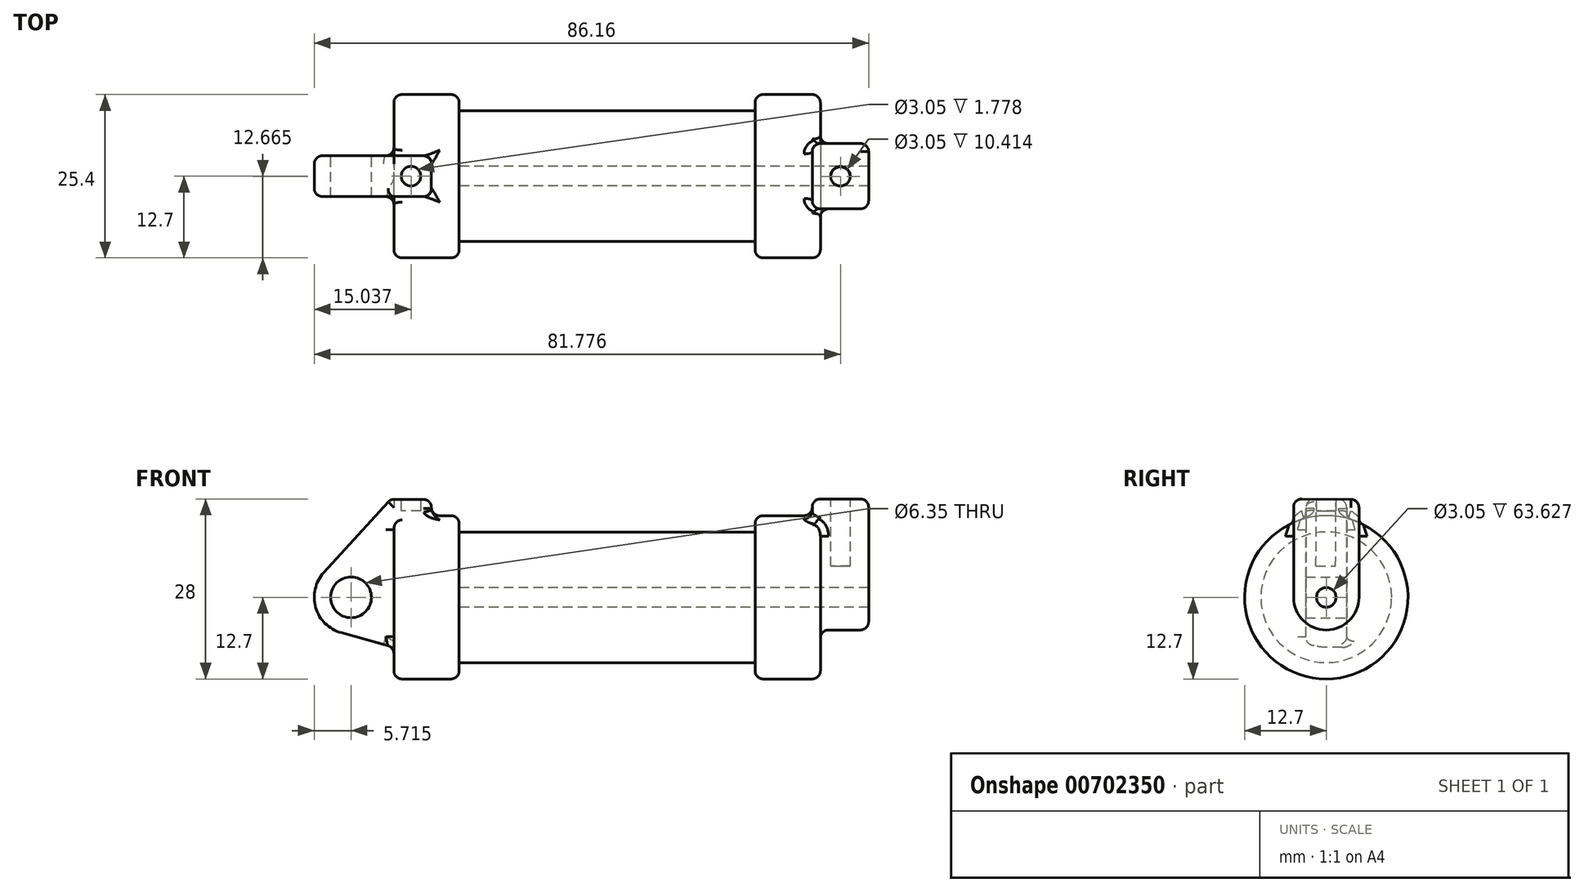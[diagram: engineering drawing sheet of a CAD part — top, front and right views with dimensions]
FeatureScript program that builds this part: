
annotation { "Feature Type Name" : "Feature", "Feature Type Description" : "" }
export const myFeature = defineFeature(function(context is Context, id is Id, definition is map)
    precondition{}
    {
        {
            var Q0;
            Q0=qCreatedBy(makeId("Front.planeOp"),FACE);
            var sketch = newSketch(context, id + "F0", { "sketchPlane" : qUnion([Q0])});
            skLineSegment(sketch, "E0", {"start": v(0, 0) * mm, "end": v(0, 12.7) * mm});
            skLineSegment(sketch, "E1", {"start": v(0, 12.7) * mm, "end": v(10.16, 12.7) * mm});
            skLineSegment(sketch, "E2", {"start": v(10.16, 12.7) * mm, "end": v(10.16, 10.16) * mm});
            skLineSegment(sketch, "E3", {"start": v(10.16, 10.16) * mm, "end": v(56.13, 10.16) * mm});
            skLineSegment(sketch, "E4", {"start": v(56.13, 10.16) * mm, "end": v(56.13, 12.7) * mm});
            skLineSegment(sketch, "E5", {"start": v(56.13, 12.7) * mm, "end": v(66.3, 12.7) * mm});
            skLineSegment(sketch, "E6", {"start": v(66.3, 12.7) * mm, "end": v(66.3, 0) * mm});
            skLineSegment(sketch, "E7", {"start": v(66.3, 0) * mm, "end": v(0, 0) * mm});
            skLineSegment(sketch, "E8", {"start": v(5.84, 15.24) * mm, "end": v(-0.5, 15.24) * mm});
            skLineSegment(sketch, "E9", {"start": v(-0.5, 15.24) * mm, "end": v(-10.88, 3.85) * mm});
            skLineSegment(sketch, "E10", {"start": v(0, 0) * mm, "end": v(-6.65, 0) * mm});
            skCircle(sketch, "E11", {"center": v(-6.65, 0) * mm, "radius": 5.72 * mm});
            skCircle(sketch, "E12", {"center": v(-6.65, 0) * mm, "radius": 3.18 * mm});
            skLineSegment(sketch, "E13", {"start": v(5.84, 15.24) * mm, "end": v(5.84, -9.4) * mm});
            skLineSegment(sketch, "E14", {"start": v(5.84, -9.4) * mm, "end": v(-8.18, -5.5) * mm});
            skSolve(sketch);
        }
        {
            var Q0;
            {var subQ0=sQuery(id+"F0.wireOp",EDGE,"E0");Q0=makeQuery(id+"F0.imprint","IMPRINT",FACE,{"disambiguationData":[TD([[makeQuery(id+"F0.imprint","IMPRINT",EDGE,{"derivedFrom":subQ0}),-1.0]])]});}
            var Q1;
            {var subQ1=sQuery(id+"F0.wireOp",EDGE,"E0");Q1=makeQuery(id+"F0.imprint","IMPRINT",FACE,{"disambiguationData":[TD([[makeQuery(id+"F0.imprint","IMPRINT",EDGE,{"derivedFrom":subQ1}),1.0]])]});}
            var Q2;
            {var subQ0=sQuery(id+"F0.wireOp",EDGE,"E14");Q2=makeQuery(id+"F0.imprint","IMPRINT",FACE,{"disambiguationData":[TD([[makeQuery(id+"F0.imprint","IMPRINT",EDGE,{"derivedFrom":subQ0}),-1.0]])]});}
            var Q3;
            {var subQ5=sQuery(id+"F0.wireOp",EDGE,"E12");Q3=makeQuery(id+"F0.imprint","IMPRINT",FACE,{"disambiguationData":[TD([[makeQuery(id+"F0.imprint","IMPRINT",EDGE,{"derivedFrom":subQ5}),-1.0]])]});}
            extrude(context, id + "F1", {"entities" : qUnion([Q0, Q1, Q2, Q3]), "endBound" : BoundingType.SYMMETRIC, "depth" : 6.35 * mm, "offsetDistance" : 25.4 * mm});
        }
        {
            var Q0;
            {var subQ0=sQuery(id+"F0.wireOp",EDGE,"E0");Q0=makeQuery(id+"F0.imprint","IMPRINT",FACE,{"disambiguationData":[TD([[makeQuery(id+"F0.imprint","IMPRINT",EDGE,{"derivedFrom":subQ0}),-1.0]])]});}
            var Q1;
            {var subQ0=sQuery(id+"F0.wireOp",EDGE,"E2");Q1=makeQuery(id+"F0.imprint","IMPRINT",FACE,{"disambiguationData":[TD([[makeQuery(id+"F0.imprint","IMPRINT",EDGE,{"derivedFrom":subQ0}),-1.0]])]});}
            var Q2;
            Q2=sQuery(id+"F0.wireOp",EDGE,"E7");
            revolve(context, id + "F2", {"operationType" : NewBodyOperationType.ADD, "entities" : qUnion([Q0, Q1]), "axis" : qUnion([Q2]), "revolveType" : RevolveType.FULL});
        }
        {
            var Q0;
            Q0=makeQuery(id+"F2.opRevolve","SWEPT_FACE",FACE,{"disambiguationData":[OSD([sQuery(id+"F0.wireOp",EDGE,"E6")])]});
            var sketch = newSketch(context, id + "F3", { "sketchPlane" : qUnion([Q0])});
            skCircle(sketch, "E15", {"center": v(0, 0) * mm, "radius": 1.52 * mm});
            skCircle(sketch, "E16", {"center": v(0, 0) * mm, "radius": 5.08 * mm});
            skLineSegment(sketch, "E17", {"start": v(-5.08, 0) * mm, "end": v(-5.08, 15.3) * mm});
            skLineSegment(sketch, "E18", {"start": v(5.08, 0) * mm, "end": v(5.08, 15.24) * mm});
            skLineSegment(sketch, "E19", {"start": v(-5.08, 15.3) * mm, "end": v(5.08, 15.24) * mm});
            skSolve(sketch);
        }
        {
            var Q0;
            {var subQ2=sQuery(id+"F3.wireOp",EDGE,"E19");Q0=makeQuery(id+"F3.imprint","IMPRINT",FACE,{"disambiguationData":[TD([[makeQuery(id+"F3.imprint","IMPRINT",EDGE,{"derivedFrom":subQ2}),-1.0]])]});}
            var Q1;
            {var subQ3=sQuery(id+"F0.wireOp",EDGE,"E6");var subQ11=makeQuery(id+"F1.opExtrude","CAP_EDGE",EDGE,{"disambiguationData":[OSD([subQ3])],"isStart":true});Q1=makeQuery(id+"F3.imprint","IMPRINT",FACE,{"disambiguationData":[TD([[makeQuery(id+"F3.imprint","IMPRINT",EDGE,{"derivedFrom":subQ11}),-1.0]])]});}
            var Q2;
            Q2=makeQuery(id+"F3.imprint","IMPRINT",FACE,{"disambiguationData":[TD([[makeQuery(id+"F3.imprint","IMPRINT",EDGE,{"derivedFrom":sQuery(id+"F3.wireOp",EDGE,"E15")}),-1.0]])]});
            var Q3;
            {var subQ0=sQuery(id+"F3.wireOp",EDGE,"E17");var subQ1=sQuery(id+"F3.wireOp",EDGE,"E16");var subQ2=makeQuery(id+"F3.imprint","INTERSECT",VERTEX,{"derivedFrom":[subQ1,subQ0]});Q3=makeQuery(id+"F3.imprint","IMPRINT",FACE,{"disambiguationData":[TD([[makeQuery(id+"F3.imprint","IMPRINT",EDGE,{"disambiguationData":[TD([[subQ2,1.0]])],"derivedFrom":subQ1}),-1.0]])]});}
            extrude(context, id + "F4", {"entities" : qUnion([Q0, Q1, Q2, Q3]), "operationType" : NewBodyOperationType.ADD, "depth" : 7.5 * mm, "offsetDistance" : 25.4 * mm, "hasSecondDirection" : true, "secondDirectionOppositeDirection" : true, "secondDirectionDepth" : 1.27 * mm});
        }
        {
            var Q0;
            {var subQ0=sQuery(id+"F0.wireOp",EDGE,"E6");Q0=makeQuery(id+"F4.boolean.opBoolean","SPLIT",FACE,{"disambiguationData":[TD([makeQuery(id+"F4.opExtrude","SWEPT_FACE",FACE,{"disambiguationData":[OSD([sQuery(id+"F3.wireOp",EDGE,"E15")])]})])],"derivedFrom":makeQuery(id+"F2.boolean.opBoolean","MERGE",FACE,{"derivedFrom":[makeQuery(id+"F1.opExtrude","SWEPT_FACE",FACE,{"disambiguationData":[OSD([subQ0])]}),makeQuery(id+"F2.opRevolve","SWEPT_FACE",FACE,{"disambiguationData":[OSD([subQ0])]})]})});}
            var Q1;
            {var subQ0=sQuery(id+"F0.wireOp",EDGE,"E2");Q1=makeQuery(id+"F2.boolean.opBoolean","MERGE",FACE,{"derivedFrom":[makeQuery(id+"F1.opExtrude","SWEPT_FACE",FACE,{"disambiguationData":[OSD([subQ0])]}),makeQuery(id+"F2.opRevolve","SWEPT_FACE",FACE,{"disambiguationData":[OSD([subQ0])]})]});}
            extrude(context, id + "F5", {"entities" : qUnion([Q0]), "operationType" : NewBodyOperationType.REMOVE, "endBound" : BoundingType.UP_TO_SURFACE, "oppositeDirection" : true, "depth" : 25.4 * mm, "endBoundEntityFace" : qUnion([Q1]), "offsetDistance" : 25.4 * mm});
        }
        {
            var Q0;
            Q0=makeQuery(id+"F1.opExtrude","SWEPT_FACE",FACE,{"disambiguationData":[OSD([sQuery(id+"F0.wireOp",EDGE,"E8")])]});
            var sketch = newSketch(context, id + "F6", { "sketchPlane" : qUnion([Q0])});
            skCircle(sketch, "E20", {"center": v(2.67, 0) * mm, "radius": 1.52 * mm});
            skPoint(sketch, "E20.centerSnap0", {"position": v(2.67, 3.18) * mm});
            skPoint(sketch, "E20.centerSnap1", {"position": v(-0.5, 0) * mm});
            skSolve(sketch);
        }
        {
            var Q0;
            Q0=makeQuery(id+"F4.opExtrude","SWEPT_FACE",FACE,{"disambiguationData":[OSD([sQuery(id+"F3.wireOp",EDGE,"E19")])]});
            var sketch = newSketch(context, id + "F7", { "sketchPlane" : qUnion([Q0])});
            skCircle(sketch, "E21", {"center": v(69.4, -0.1) * mm, "radius": 1.52 * mm});
            skPoint(sketch, "E21.centerSnap0", {"position": v(73.79, -0.1) * mm});
            skPoint(sketch, "E21.centerSnap1", {"position": v(69.4, 4.98) * mm});
            skSolve(sketch);
        }
        {
            var Q0;
            Q0 = qSketchRegion(id + "F6", true);
            extrude(context, id + "F8", {"entities" : qUnion([Q0]), "operationType" : NewBodyOperationType.REMOVE, "oppositeDirection" : true, "depth" : 1.78 * mm, "offsetDistance" : 25.4 * mm});
        }
        {
            var Q0;
            Q0 = qSketchRegion(id + "F7", true);
            extrude(context, id + "F9", {"entities" : qUnion([Q0]), "operationType" : NewBodyOperationType.REMOVE, "oppositeDirection" : true, "depth" : 10.4 * mm, "offsetDistance" : 25.4 * mm});
        }
        {
            var Q0;
            Q0=makeQuery(id+"F2.opRevolve","SWEPT_EDGE",EDGE,{"disambiguationData":[OSD([sQuery(id+"F0.wireOp",EDGE,"E1"),sQuery(id+"F0.wireOp",EDGE,"E2")])]});
            fillet(context, id + "F10", {"entities" : qUnion([Q0]), "radius" : 1.27 * mm, "tangentPropagation" : true, "allowEdgeOverflow" : false});
        }
        {
            var Q0;
            Q0=makeQuery(id+"F2.opRevolve","SWEPT_EDGE",EDGE,{"disambiguationData":[OSD([sQuery(id+"F0.wireOp",EDGE,"E4"),sQuery(id+"F0.wireOp",EDGE,"E5")])]});
            fillet(context, id + "F11", {"entities" : qUnion([Q0]), "radius" : 1.27 * mm, "tangentPropagation" : true, "allowEdgeOverflow" : false});
        }
        {
            var Q0;
            Q0=makeQuery(id+"F4.opExtrude","SWEPT_EDGE",EDGE,{"disambiguationData":[OSD([sQuery(id+"F3.wireOp",EDGE,"E17"),sQuery(id+"F3.wireOp",EDGE,"E19")])]});
            fillet(context, id + "F12", {"entities" : qUnion([Q0]), "radius" : 1.27 * mm, "tangentPropagation" : true, "allowEdgeOverflow" : false});
        }
        {
            var Q0;
            Q0=makeQuery(id+"F4.opExtrude","CAP_EDGE",EDGE,{"disambiguationData":[OSD([sQuery(id+"F3.wireOp",EDGE,"E19")])],"isStart":false});
            fillet(context, id + "F13", {"entities" : qUnion([Q0]), "radius" : 1.27 * mm, "tangentPropagation" : true, "allowEdgeOverflow" : false});
        }
        {
            var Q0;
            Q0=makeQuery(id+"F2.opRevolve","SWEPT_EDGE",EDGE,{"disambiguationData":[OSD([sQuery(id+"F0.wireOp",EDGE,"E5"),sQuery(id+"F0.wireOp",EDGE,"E6")])]});
            fillet(context, id + "F14", {"entities" : qUnion([Q0]), "radius" : 1.27 * mm, "tangentPropagation" : true, "allowEdgeOverflow" : false});
        }
        {
            var Q0;
            Q0=makeQuery(id+"F4.opExtrude","SWEPT_EDGE",EDGE,{"disambiguationData":[OSD([sQuery(id+"F3.wireOp",EDGE,"E18"),sQuery(id+"F3.wireOp",EDGE,"E19")])]});
            fillet(context, id + "F15", {"entities" : qUnion([Q0]), "radius" : 1.27 * mm, "tangentPropagation" : true, "allowEdgeOverflow" : false});
        }
        {
            var Q0;
            Q0=makeQuery(id+"F4.boolean.opBoolean","INTERSECT",EDGE,{"derivedFrom":[makeQuery(id+"F2.opRevolve","SWEPT_FACE",FACE,{"disambiguationData":[OSD([sQuery(id+"F0.wireOp",EDGE,"E6")])]}),makeQuery(id+"F4.opExtrude","SWEPT_FACE",FACE,{"disambiguationData":[OSD([sQuery(id+"F3.wireOp",EDGE,"E17")])]})]});
            fillet(context, id + "F16", {"entities" : qUnion([Q0]), "radius" : 1.27 * mm, "tangentPropagation" : true, "allowEdgeOverflow" : false});
        }
        {
            var Q0;
            Q0=makeQuery(id+"F1.opExtrude","CAP_EDGE",EDGE,{"disambiguationData":[OSD([sQuery(id+"F0.wireOp",EDGE,"E8")])],"isStart":true});
            fillet(context, id + "F17", {"entities" : qUnion([Q0]), "radius" : 1.27 * mm, "tangentPropagation" : true, "allowEdgeOverflow" : false});
        }
        {
            var Q0;
            Q0=makeQuery(id+"F1.opExtrude","CAP_EDGE",EDGE,{"disambiguationData":[OSD([sQuery(id+"F0.wireOp",EDGE,"E9")])],"isStart":false});
            var Q1;
            Q1=makeQuery(id+"F2.boolean.opBoolean","INTERSECT",EDGE,{"derivedFrom":[makeQuery(id+"F1.opExtrude","CAP_FACE",FACE,{"disambiguationData":[OSD([sQuery(id+"F0.wireOp",EDGE,"E8"),sQuery(id+"F0.wireOp",EDGE,"E9"),sQuery(id+"F0.wireOp",EDGE,"E11"),sQuery(id+"F0.wireOp",EDGE,"E12"),sQuery(id+"F0.wireOp",EDGE,"E13"),sQuery(id+"F0.wireOp",EDGE,"E14")])],"isStart":false}),makeQuery(id+"F2.opRevolve","SWEPT_FACE",FACE,{"disambiguationData":[OSD([sQuery(id+"F0.wireOp",EDGE,"E0")])]})]});
            fillet(context, id + "F18", {"entities" : qUnion([Q0, Q1]), "radius" : 1.27 * mm, "tangentPropagation" : true, "allowEdgeOverflow" : false});
        }
        {
            var Q0;
            Q0=makeQuery(id+"F2.boolean.opBoolean","INTERSECT",EDGE,{"derivedFrom":[makeQuery(id+"F1.opExtrude","CAP_FACE",FACE,{"disambiguationData":[OSD([sQuery(id+"F0.wireOp",EDGE,"E8"),sQuery(id+"F0.wireOp",EDGE,"E9"),sQuery(id+"F0.wireOp",EDGE,"E11"),sQuery(id+"F0.wireOp",EDGE,"E12"),sQuery(id+"F0.wireOp",EDGE,"E13"),sQuery(id+"F0.wireOp",EDGE,"E14")])],"isStart":true}),makeQuery(id+"F2.opRevolve","SWEPT_FACE",FACE,{"disambiguationData":[OSD([sQuery(id+"F0.wireOp",EDGE,"E0")])]})]});
            fillet(context, id + "F19", {"entities" : qUnion([Q0]), "radius" : 1.27 * mm, "tangentPropagation" : true, "allowEdgeOverflow" : false});
        }
        {
            var Q0;
            Q0=makeQuery(id+"F1.opExtrude","CAP_EDGE",EDGE,{"disambiguationData":[OSD([sQuery(id+"F0.wireOp",EDGE,"E9")])],"isStart":true});
            fillet(context, id + "F20", {"entities" : qUnion([Q0]), "radius" : 1.27 * mm, "tangentPropagation" : true, "allowEdgeOverflow" : false});
        }
        {
            var Q0;
            Q0=makeQuery(id+"F2.opRevolve","SWEPT_EDGE",EDGE,{"disambiguationData":[OSD([sQuery(id+"F0.wireOp",EDGE,"E0"),sQuery(id+"F0.wireOp",EDGE,"E1")])]});
            fillet(context, id + "F21", {"entities" : qUnion([Q0]), "radius" : 1.27 * mm, "tangentPropagation" : true, "allowEdgeOverflow" : false});
        }
        {
            var Q0;
            Q0=makeQuery(id+"F2.boolean.opBoolean","INTERSECT",EDGE,{"derivedFrom":[makeQuery(id+"F1.opExtrude","CAP_FACE",FACE,{"disambiguationData":[OSD([sQuery(id+"F0.wireOp",EDGE,"E8"),sQuery(id+"F0.wireOp",EDGE,"E9"),sQuery(id+"F0.wireOp",EDGE,"E11"),sQuery(id+"F0.wireOp",EDGE,"E12"),sQuery(id+"F0.wireOp",EDGE,"E13"),sQuery(id+"F0.wireOp",EDGE,"E14")])],"isStart":false}),makeQuery(id+"F2.opRevolve","SWEPT_FACE",FACE,{"disambiguationData":[OSD([sQuery(id+"F0.wireOp",EDGE,"E1")])]})]});
            fillet(context, id + "F22", {"entities" : qUnion([Q0]), "radius" : 1.27 * mm, "tangentPropagation" : true, "allowEdgeOverflow" : false});
        }
        {
            var Q0;
            {var subQ0=makeQuery(id+"F1.opExtrude","CAP_FACE",FACE,{"disambiguationData":[OSD([sQuery(id+"F0.wireOp",EDGE,"E8"),sQuery(id+"F0.wireOp",EDGE,"E9"),sQuery(id+"F0.wireOp",EDGE,"E11"),sQuery(id+"F0.wireOp",EDGE,"E12"),sQuery(id+"F0.wireOp",EDGE,"E13"),sQuery(id+"F0.wireOp",EDGE,"E14")])],"isStart":true});Q0=makeQuery(id+"F21.opFillet","BLEND_EDGE",EDGE,{"blendedFrom":[makeQuery(id+"F19.opFillet","BLEND_EDGE",EDGE,{"blendedFrom":[makeQuery(id+"F2.boolean.opBoolean","INTERSECT",EDGE,{"derivedFrom":[subQ0,makeQuery(id+"F2.opRevolve","SWEPT_FACE",FACE,{"disambiguationData":[OSD([sQuery(id+"F0.wireOp",EDGE,"E0")])]})]}),makeQuery(id+"F2.opRevolve","SWEPT_FACE",FACE,{"disambiguationData":[OSD([sQuery(id+"F0.wireOp",EDGE,"E1")])]})],"blendedInto":[makeQuery(id+"F2.opRevolve","SWEPT_FACE",FACE,{"disambiguationData":[OSD([sQuery(id+"F0.wireOp",EDGE,"E1")])]})]}),subQ0],"blendedInto":[subQ0]});}
            fillet(context, id + "F23", {"entities" : qUnion([Q0]), "radius" : 1.27 * mm, "tangentPropagation" : true, "allowEdgeOverflow" : false});
        }
        {
            var Q0;
            Q0=makeQuery(id+"F2.boolean.opBoolean","INTERSECT",EDGE,{"derivedFrom":[makeQuery(id+"F1.opExtrude","SWEPT_FACE",FACE,{"disambiguationData":[OSD([sQuery(id+"F0.wireOp",EDGE,"E13")])]}),makeQuery(id+"F2.opRevolve","SWEPT_FACE",FACE,{"disambiguationData":[OSD([sQuery(id+"F0.wireOp",EDGE,"E1")])]})]});
            fillet(context, id + "F24", {"entities" : qUnion([Q0]), "radius" : 1.27 * mm, "tangentPropagation" : true, "allowEdgeOverflow" : false});
        }
        {
            var Q0;
            Q0=makeQuery(id+"F1.opExtrude","SWEPT_EDGE",EDGE,{"disambiguationData":[OSD([sQuery(id+"F0.wireOp",EDGE,"E8"),sQuery(id+"F0.wireOp",EDGE,"E13")])]});
            fillet(context, id + "F25", {"entities" : qUnion([Q0]), "radius" : 1.27 * mm, "tangentPropagation" : true, "allowEdgeOverflow" : false});
        }
        {
            var Q0;
            Q0=makeQuery(id+"F4.opExtrude","CAP_EDGE",EDGE,{"disambiguationData":[OSD([sQuery(id+"F3.wireOp",EDGE,"E19")])],"isStart":true});
            fillet(context, id + "F26", {"entities" : qUnion([Q0]), "radius" : 1.27 * mm, "tangentPropagation" : true, "allowEdgeOverflow" : false});
        }
        {
            var Q0;
            Q0=makeQuery(id+"F4.boolean.opBoolean","INTERSECT",EDGE,{"derivedFrom":[makeQuery(id+"F2.opRevolve","SWEPT_FACE",FACE,{"disambiguationData":[OSD([sQuery(id+"F0.wireOp",EDGE,"E5")])]}),makeQuery(id+"F4.opExtrude","CAP_FACE",FACE,{"disambiguationData":[OSD([sQuery(id+"F3.wireOp",EDGE,"E15"),sQuery(id+"F3.wireOp",EDGE,"E16"),sQuery(id+"F3.wireOp",EDGE,"E17"),sQuery(id+"F3.wireOp",EDGE,"E18"),sQuery(id+"F3.wireOp",EDGE,"E19")])],"isStart":true})]});
            fillet(context, id + "F27", {"entities" : qUnion([Q0]), "radius" : 1.27 * mm, "tangentPropagation" : true, "allowEdgeOverflow" : false});
        }
    });
